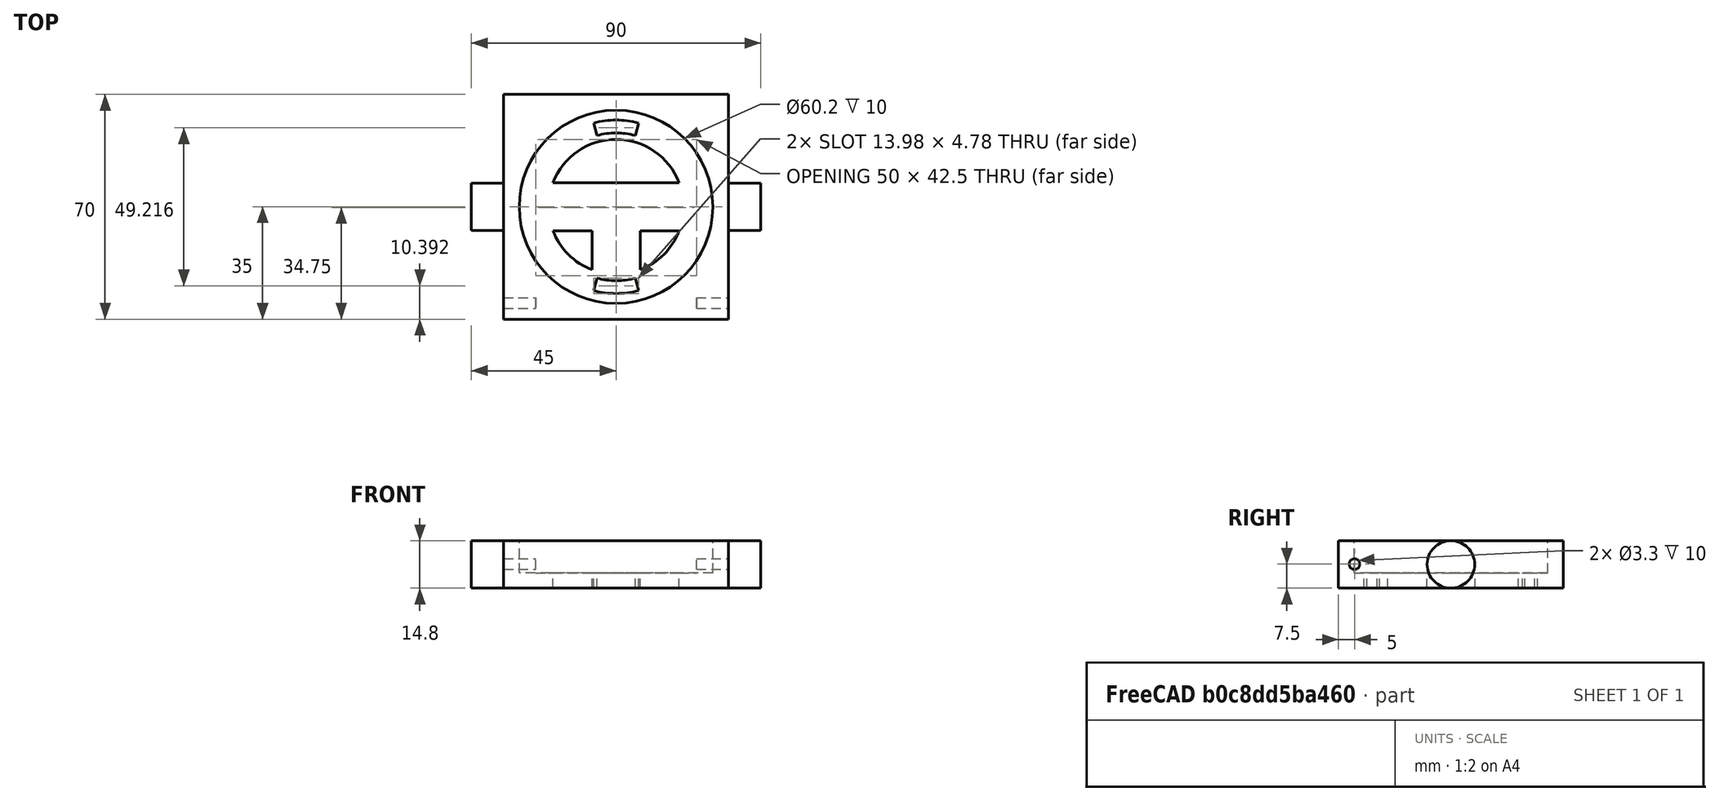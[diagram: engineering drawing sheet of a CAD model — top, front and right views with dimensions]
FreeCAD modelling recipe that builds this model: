
FCSTD DOCUMENT  (FreeCAD 0.18R4 (GitTag))
Label: Kamerhalter_Teil_2
License: All rights reserved
LicenseURL: http://en.wikipedia.org/wiki/All_rights_reserved
objects: Part::Cylinder×10, Part::Cut×4, Part::Box×3, Part::MultiFuse×3
note: 20 computed .brp shape members not serialized (recipe doc carries the construction recipe); baked Part::Feature solids carry a one-line shape summary decoded from their .brp

FEATURE [Part::Box] Box  label="Würfel"
  AttacherType = Attacher::AttachEngine3D
  Height = 14.8
  Length = 70
  Placement = pos=(-35,-35,0) rot=(0,0,1;0rad)
  Width = 70
FEATURE [Part::Cylinder] Cylinder001  label="Zylinder001"
  Angle = 30
  AttacherType = Attacher::AttachEngine3D
  Height = 4.8
  Radius = 27
FEATURE [Part::Cylinder] Cylinder002  label="Zylinder002"
  Angle = 30
  AttacherType = Attacher::AttachEngine3D
  Height = 4.8
  Radius = 23
FEATURE [Part::Cut] Cut001  label="Cut004"
  Base = -> Cylinder001
  Placement = pos=(0,0,0) rot=(0,0,-1;1.8326rad)
  Tool = -> Cylinder002
FEATURE [Part::Cylinder] Cylinder003  label="Zylinder003"
  Angle = 30
  AttacherType = Attacher::AttachEngine3D
  Height = 4.8
  Radius = 27
FEATURE [Part::Cylinder] Cylinder004  label="Zylinder004"
  Angle = 30
  AttacherType = Attacher::AttachEngine3D
  Height = 4.8
  Radius = 23
FEATURE [Part::Cut] Cut002  label="Cut003"
  Base = -> Cylinder003
  Placement = pos=(0,0,0) rot=(0,0,1;1.309rad)
  Tool = -> Cylinder004
FEATURE [Part::Cylinder] Cylinder005  label="Noppen_001"
  Angle = 360
  AttacherType = Attacher::AttachEngine3D
  Height = 10
  Placement = pos=(-45,0,7.4) rot=(0,1,0;1.5708rad)
  Radius = 7.4
FEATURE [Part::Cylinder] Cylinder006  label="Noppen_002"
  Angle = 360
  AttacherType = Attacher::AttachEngine3D
  Height = 10
  Placement = pos=(35,0,7.4) rot=(0,1,0;1.5708rad)
  Radius = 7.4
FEATURE [Part::Cylinder] Cylinder010  label="Bohrloch_001"
  Angle = 360
  AttacherType = Attacher::AttachEngine3D
  Height = 10
  Placement = pos=(-35,-30,7.5) rot=(0,1,0;1.5708rad)
  Radius = 1.65
FEATURE [Part::Cylinder] Cylinder012  label="Bohrloch_002"
  Angle = 360
  AttacherType = Attacher::AttachEngine3D
  Height = 10
  Placement = pos=(25,-30,7.5) rot=(0,1,0;1.5708rad)
  Radius = 1.65
FEATURE [Part::Cylinder] Cylinder  label="Zylinder"
  Angle = 360
  AttacherType = Attacher::AttachEngine3D
  Height = 10
  Placement = pos=(0,0,4.8) rot=(0,0,1;0rad)
  Radius = 30.1
FEATURE [Part::Cut] Cut  label="Cut002"
  Base = -> Box
  Tool = -> Cylinder
FEATURE [Part::Cylinder] Cylinder013  label="Bohrloch_003"
  Angle = 360
  AttacherType = Attacher::AttachEngine3D
  Height = 4.8
  Radius = 21
FEATURE [Part::MultiFuse] Fusion  label="Bohrschlitze"
  Shapes = -> [Cut002,Cut001,Cylinder010,Cylinder012,Cylinder013]
FEATURE [Part::Cut] Cut003  label="Cut001"
  Base = -> Cut
  Tool = -> Fusion
FEATURE [Part::Box] Box001  label="Würfel001"
  AttacherType = Attacher::AttachEngine3D
  Height = 4.8
  Length = 50
  Placement = pos=(-25,-7.5,0) rot=(0,0,1;0rad)
  Width = 15
FEATURE [Part::Box] Box002  label="Würfel002"
  AttacherType = Attacher::AttachEngine3D
  Height = 4.8
  Length = 15
  Placement = pos=(-7.5,-21.5,0) rot=(0,0,1;0rad)
  Width = 21.5
FEATURE [Part::MultiFuse] Fusion001
  Shapes = -> [Cylinder005,Box001,Cylinder006,Box002]
FEATURE [Part::MultiFuse] Fusion002
  Shapes = -> [Cut003,Fusion001]
